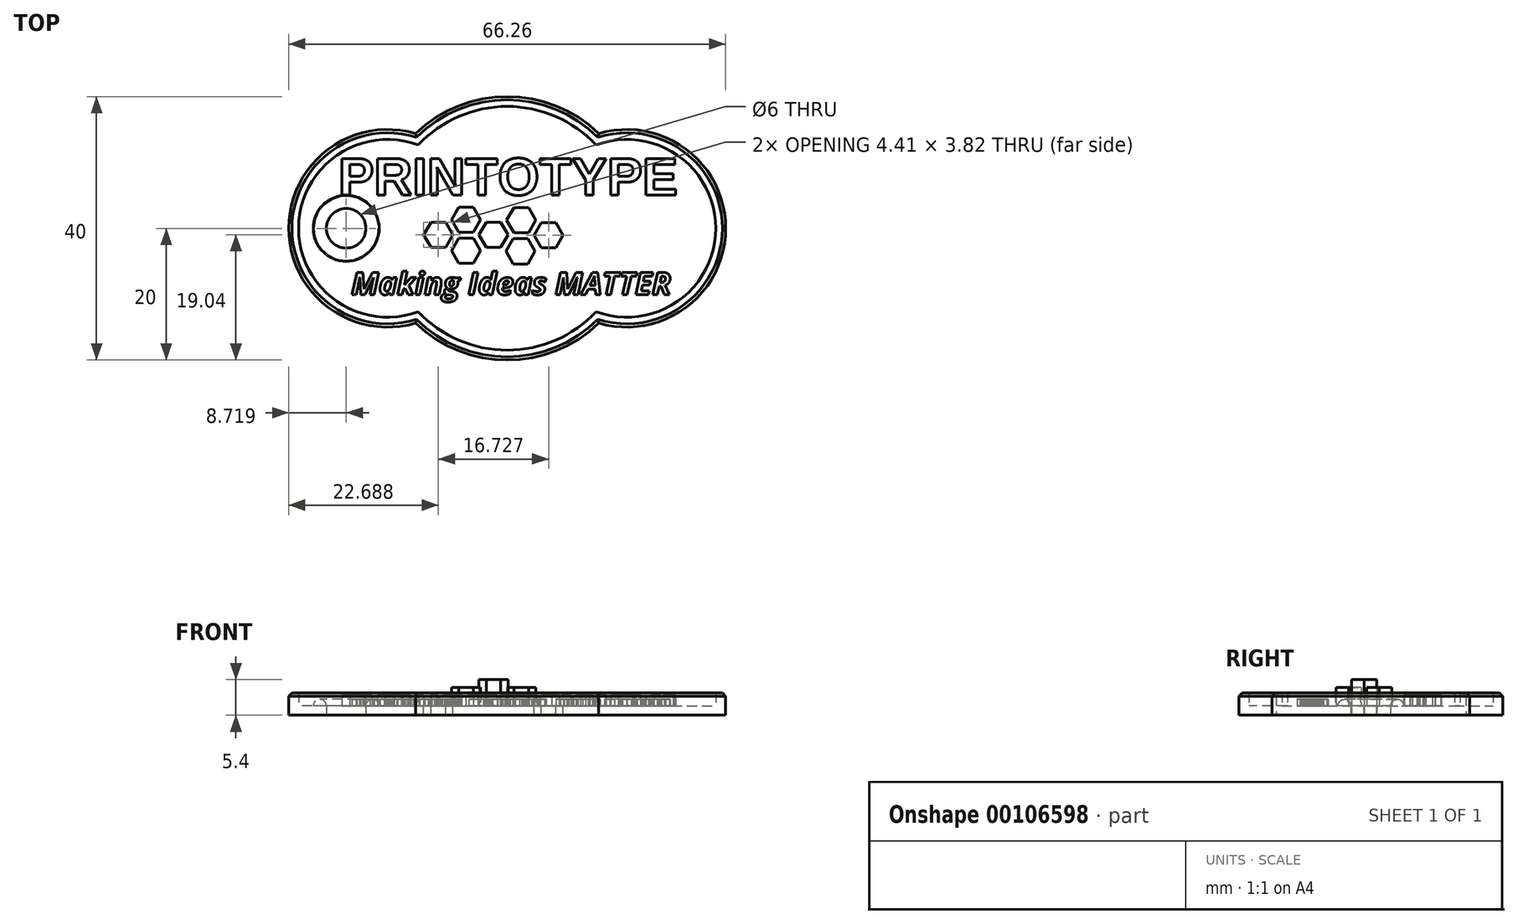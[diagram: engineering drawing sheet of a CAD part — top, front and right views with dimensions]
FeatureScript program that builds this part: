
annotation { "Feature Type Name" : "Feature", "Feature Type Description" : "" }
export const myFeature = defineFeature(function(context is Context, id is Id, definition is map)
    precondition{}
    {
        {
            var Q0;
            Q0=qCreatedBy(makeId("Top.planeOp"),FACE);
            var sketch = newSketch(context, id + "F0", { "sketchPlane" : qUnion([Q0])});
            skArc(sketch, "E0", {"start": v(-13.9, 14.39) * mm, "mid": v(-33.13, 0) * mm, "end": v(-13.9, -14.39) * mm});
            skLineSegment(sketch, "E1", {"start": v(0, 0) * mm, "end": v(0, 52.6) * mm});
            skArc(sketch, "E2.MirrorC", {"start": v(13.9, 14.39) * mm, "mid": v(33.13, 0) * mm, "end": v(13.9, -14.39) * mm});
            skCircle(sketch, "E3", {"center": v(-24.41, 0) * mm, "radius": 3 * mm});
            skCircle(sketch, "E4", {"center": v(-24.41, 0) * mm, "radius": 5 * mm});
            skArc(sketch, "E5", {"start": v(-13.48, 12.67) * mm, "mid": v(-31.63, 0) * mm, "end": v(-13.48, -12.67) * mm});
            skArc(sketch, "E6", {"start": v(13.48, -12.67) * mm, "mid": v(31.63, 0) * mm, "end": v(13.48, 12.67) * mm});
            skArc(sketch, "E7", {"start": v(-13.48, -12.67) * mm, "mid": v(0, -18.5) * mm, "end": v(13.48, -12.67) * mm});
            skArc(sketch, "E8.trimOffspring", {"start": v(-13.9, -14.39) * mm, "mid": v(0, -20) * mm, "end": v(13.9, -14.39) * mm});
            skArc(sketch, "E9.trimOffspring", {"start": v(13.48, 12.67) * mm, "mid": v(0, 18.5) * mm, "end": v(-13.48, 12.67) * mm});
            skArc(sketch, "E10.trimOffspring", {"start": v(13.9, 14.39) * mm, "mid": v(0, 20) * mm, "end": v(-13.9, 14.39) * mm});
            skSolve(sketch);
        }
        {
            var Q0;
            Q0=qCreatedBy(makeId("Top.planeOp"),FACE);
            var sketch = newSketch(context, id + "F1", { "sketchPlane" : qUnion([Q0])});
            skText(sketch, "E11", { "text": "PRINTOTYPE", "fontName": "Arimo-Bold.ttf"});
            const initialGuessF1  = {"E11": [-0.02558, 0.00505, 1, 0, 0.0058]};
            skSetInitialGuess(sketch, initialGuessF1);
            skSolve(sketch);
        }
        {
            var Q0;
            Q0=qCreatedBy(makeId("Top.planeOp"),FACE);
            var sketch = newSketch(context, id + "F2", { "sketchPlane" : qUnion([Q0])});
            skText(sketch, "E12", { "text": "Making Ideas MATTER", "fontName": "OpenSans-BoldItalic.ttf"});
            const initialGuessF2  = {"E12": [-0.02364, -0.01007, 1, 0, 0.0034]};
            skSetInitialGuess(sketch, initialGuessF2);
            skSolve(sketch);
        }
        {
            var Q0;
            Q0=makeQuery(id+"F0.imprint","IMPRINT",FACE,{"disambiguationData":[TD([[makeQuery(id+"F0.imprint","IMPRINT",EDGE,{"derivedFrom":sQuery(id+"F0.wireOp",EDGE,"E4")}),-1.0]])]});
            var Q1;
            {var subQ5=sQuery(id+"F0.wireOp",EDGE,"E0");Q1=makeQuery(id+"F0.imprint","IMPRINT",FACE,{"disambiguationData":[TD([[makeQuery(id+"F0.imprint","IMPRINT",EDGE,{"derivedFrom":subQ5}),1.0]])]});}
            var Q2;
            Q2=makeQuery(id+"F0.imprint","IMPRINT",FACE,{"disambiguationData":[TD([[makeQuery(id+"F0.imprint","IMPRINT",EDGE,{"derivedFrom":sQuery(id+"F0.wireOp",EDGE,"E3")}),-1.0]])]});
            extrude(context, id + "F3", {"entities" : qUnion([Q0, Q1, Q2]), "depth" : 1.4 * mm});
        }
        {
            var Q0;
            Q0=makeQuery(id+"F0.imprint","IMPRINT",FACE,{"disambiguationData":[TD([[makeQuery(id+"F0.imprint","IMPRINT",EDGE,{"derivedFrom":sQuery(id+"F0.wireOp",EDGE,"E3")}),-1.0]])]});
            var Q1;
            {var subQ5=sQuery(id+"F0.wireOp",EDGE,"E0");Q1=makeQuery(id+"F0.imprint","IMPRINT",FACE,{"disambiguationData":[TD([[makeQuery(id+"F0.imprint","IMPRINT",EDGE,{"derivedFrom":subQ5}),1.0]])]});}
            extrude(context, id + "F4", {"entities" : qUnion([Q0, Q1]), "operationType" : NewBodyOperationType.ADD, "depth" : 3.4 * mm});
        }
        {
            var Q0;
            Q0=makeQuery(id+"F4.opExtrude","CAP_EDGE",EDGE,{"disambiguationData":[OSD([sQuery(id+"F0.wireOp",EDGE,"E4")])],"isStart":false});
            fillet(context, id + "F5", {"entities" : qUnion([Q0]), "radius" : 2 * mm, "tangentPropagation" : true, "allowEdgeOverflow" : false});
        }
        {
            var Q0;
            {var subQ0=sQuery(id+"F0.wireOp",EDGE,"E3");Q0=makeQuery(id+"F5.opFillet","BLEND_EDGE",EDGE,{"blendedFrom":[makeQuery(id+"F4.opExtrude","CAP_EDGE",EDGE,{"disambiguationData":[OSD([sQuery(id+"F0.wireOp",EDGE,"E4")])],"isStart":false}),makeQuery(id+"F4.boolean.opBoolean","MERGE",FACE,{"derivedFrom":[makeQuery(id+"F3.opExtrude","SWEPT_FACE",FACE,{"disambiguationData":[OSD([subQ0])]}),makeQuery(id+"F4.opExtrude","SWEPT_FACE",FACE,{"disambiguationData":[OSD([subQ0])]})]})],"blendedInto":[makeQuery(id+"F4.boolean.opBoolean","MERGE",FACE,{"derivedFrom":[makeQuery(id+"F3.opExtrude","SWEPT_FACE",FACE,{"disambiguationData":[OSD([subQ0])]}),makeQuery(id+"F4.opExtrude","SWEPT_FACE",FACE,{"disambiguationData":[OSD([subQ0])]})]})]});}
            fillet(context, id + "F6", {"entities" : qUnion([Q0]), "radius" : 1 * mm, "tangentPropagation" : true, "allowEdgeOverflow" : false});
        }
        {
            var Q0;
            Q0 = qSketchRegion(id + "F1", true);
            extrude(context, id + "F7", {"entities" : qUnion([Q0]), "operationType" : NewBodyOperationType.ADD, "depth" : 3 * mm});
        }
        {
            var Q0;
            Q0 = qSketchRegion(id + "F2", true);
            extrude(context, id + "F8", {"entities" : qUnion([Q0]), "operationType" : NewBodyOperationType.ADD, "depth" : 2.4 * mm});
        }
        {
            var Q0;
            {var subQ36=makeQuery(id+"F4.opExtrude","SWEPT_FACE",FACE,{"disambiguationData":[OSD([sQuery(id+"F0.wireOp",EDGE,"E5")])]});var subQ58=sQuery(id+"F0.wireOp",EDGE,"E3");Q0=makeQuery(id+"F8.boolean.opBoolean","SPLIT",FACE,{"disambiguationData":[TD([subQ36])],"derivedFrom":makeQuery(id+"F7.boolean.opBoolean","SPLIT",FACE,{"disambiguationData":[TD([subQ36])],"derivedFrom":makeQuery(id+"F3.opExtrude","CAP_FACE",FACE,{"disambiguationData":[OSD([sQuery(id+"F0.wireOp",EDGE,"E0"),sQuery(id+"F0.wireOp",EDGE,"E2.MirrorC"),subQ58,sQuery(id+"F0.wireOp",EDGE,"E8.trimOffspring"),sQuery(id+"F0.wireOp",EDGE,"E10.trimOffspring")])],"isStart":false})})});}
            var sketch = newSketch(context, id + "F9", { "sketchPlane" : qUnion([Q0])});
            skCircle(sketch, "E13.cCircle", {"center": v(-10.44, -0.96) * mm, "radius": 1.91 * mm, "construction": true});
            skLineSegment(sketch, "E13.0", {"start": v(-11.55, 0.95) * mm, "end": v(-9.34, 0.95) * mm});
            skLineSegment(sketch, "E13.1", {"start": v(-9.34, 0.95) * mm, "end": v(-8.24, -0.96) * mm});
            skLineSegment(sketch, "E13.2", {"start": v(-8.24, -0.96) * mm, "end": v(-9.34, -2.87) * mm});
            skLineSegment(sketch, "E13.3", {"start": v(-9.34, -2.87) * mm, "end": v(-11.55, -2.87) * mm});
            skLineSegment(sketch, "E13.4", {"start": v(-11.55, -2.87) * mm, "end": v(-12.65, -0.96) * mm});
            skLineSegment(sketch, "E13.5", {"start": v(-12.65, -0.96) * mm, "end": v(-11.55, 0.95) * mm});
            skPoint(sketch, "E13.0.midPoint", {"position": v(-10.44, 0.95) * mm});
            skCircle(sketch, "E14.cCircle", {"center": v(-6.24, 1.29) * mm, "radius": 1.91 * mm, "construction": true});
            skLineSegment(sketch, "E14.0", {"start": v(-7.34, 3.2) * mm, "end": v(-5.13, 3.2) * mm});
            skLineSegment(sketch, "E14.1", {"start": v(-5.13, 3.2) * mm, "end": v(-4.03, 1.29) * mm});
            skLineSegment(sketch, "E14.2", {"start": v(-4.03, 1.29) * mm, "end": v(-5.13, -0.63) * mm});
            skLineSegment(sketch, "E14.3", {"start": v(-5.13, -0.63) * mm, "end": v(-7.34, -0.63) * mm});
            skLineSegment(sketch, "E14.4", {"start": v(-7.34, -0.63) * mm, "end": v(-8.44, 1.29) * mm});
            skLineSegment(sketch, "E14.5", {"start": v(-8.44, 1.29) * mm, "end": v(-7.34, 3.2) * mm});
            skPoint(sketch, "E14.0.midPoint", {"position": v(-6.24, 3.2) * mm});
            skCircle(sketch, "E15.cCircle", {"center": v(-6.24, -3.4) * mm, "radius": 1.91 * mm, "construction": true});
            skLineSegment(sketch, "E15.0", {"start": v(-7.34, -1.49) * mm, "end": v(-5.13, -1.49) * mm});
            skLineSegment(sketch, "E15.1", {"start": v(-5.13, -1.49) * mm, "end": v(-4.03, -3.4) * mm});
            skLineSegment(sketch, "E15.2", {"start": v(-4.03, -3.4) * mm, "end": v(-5.13, -5.3) * mm});
            skLineSegment(sketch, "E15.3", {"start": v(-5.13, -5.3) * mm, "end": v(-7.34, -5.3) * mm});
            skLineSegment(sketch, "E15.4", {"start": v(-7.34, -5.3) * mm, "end": v(-8.44, -3.4) * mm});
            skLineSegment(sketch, "E15.5", {"start": v(-8.44, -3.4) * mm, "end": v(-7.34, -1.49) * mm});
            skPoint(sketch, "E15.0.midPoint", {"position": v(-6.24, -1.49) * mm});
            skCircle(sketch, "E16.cCircle", {"center": v(-2.08, -1) * mm, "radius": 1.91 * mm, "construction": true});
            skLineSegment(sketch, "E16.0", {"start": v(-3.18, 0.9) * mm, "end": v(-0.98, 0.9) * mm});
            skLineSegment(sketch, "E16.1", {"start": v(-0.98, 0.9) * mm, "end": v(0.13, -1) * mm});
            skLineSegment(sketch, "E16.2", {"start": v(0.13, -1) * mm, "end": v(-0.98, -2.92) * mm});
            skLineSegment(sketch, "E16.3", {"start": v(-0.98, -2.92) * mm, "end": v(-3.18, -2.92) * mm});
            skLineSegment(sketch, "E16.4", {"start": v(-3.18, -2.92) * mm, "end": v(-4.29, -1) * mm});
            skLineSegment(sketch, "E16.5", {"start": v(-4.29, -1) * mm, "end": v(-3.18, 0.9) * mm});
            skPoint(sketch, "E16.0.midPoint", {"position": v(-2.08, 0.9) * mm});
            skCircle(sketch, "E17.cCircle", {"center": v(2.03, -3.5) * mm, "radius": 1.91 * mm, "construction": true});
            skLineSegment(sketch, "E17.0", {"start": v(0.93, -1.58) * mm, "end": v(3.14, -1.58) * mm});
            skLineSegment(sketch, "E17.1", {"start": v(3.14, -1.58) * mm, "end": v(4.24, -3.5) * mm});
            skLineSegment(sketch, "E17.2", {"start": v(4.24, -3.5) * mm, "end": v(3.14, -5.4) * mm});
            skLineSegment(sketch, "E17.3", {"start": v(3.14, -5.4) * mm, "end": v(0.93, -5.4) * mm});
            skLineSegment(sketch, "E17.4", {"start": v(0.93, -5.4) * mm, "end": v(-0.18, -3.5) * mm});
            skLineSegment(sketch, "E17.5", {"start": v(-0.18, -3.5) * mm, "end": v(0.93, -1.58) * mm});
            skPoint(sketch, "E17.0.midPoint", {"position": v(2.03, -1.58) * mm});
            skCircle(sketch, "E18.cCircle", {"center": v(2.13, 1.24) * mm, "radius": 1.91 * mm, "construction": true});
            skLineSegment(sketch, "E18.0", {"start": v(1.02, 3.15) * mm, "end": v(3.23, 3.15) * mm});
            skLineSegment(sketch, "E18.1", {"start": v(3.23, 3.15) * mm, "end": v(4.33, 1.24) * mm});
            skLineSegment(sketch, "E18.2", {"start": v(4.33, 1.24) * mm, "end": v(3.23, -0.67) * mm});
            skLineSegment(sketch, "E18.3", {"start": v(3.23, -0.67) * mm, "end": v(1.02, -0.67) * mm});
            skLineSegment(sketch, "E18.4", {"start": v(1.02, -0.67) * mm, "end": v(-0.08, 1.24) * mm});
            skLineSegment(sketch, "E18.5", {"start": v(-0.08, 1.24) * mm, "end": v(1.02, 3.15) * mm});
            skPoint(sketch, "E18.0.midPoint", {"position": v(2.13, 3.15) * mm});
            skCircle(sketch, "E19.cCircle", {"center": v(6.29, -1.05) * mm, "radius": 1.91 * mm, "construction": true});
            skLineSegment(sketch, "E19.0", {"start": v(5.18, 0.86) * mm, "end": v(7.39, 0.86) * mm});
            skLineSegment(sketch, "E19.1", {"start": v(7.39, 0.86) * mm, "end": v(8.5, -1.05) * mm});
            skLineSegment(sketch, "E19.2", {"start": v(8.5, -1.05) * mm, "end": v(7.39, -2.96) * mm});
            skLineSegment(sketch, "E19.3", {"start": v(7.39, -2.96) * mm, "end": v(5.18, -2.96) * mm});
            skLineSegment(sketch, "E19.4", {"start": v(5.18, -2.96) * mm, "end": v(4.08, -1.05) * mm});
            skLineSegment(sketch, "E19.5", {"start": v(4.08, -1.05) * mm, "end": v(5.18, 0.86) * mm});
            skPoint(sketch, "E19.0.midPoint", {"position": v(6.29, 0.86) * mm});
            skSolve(sketch);
        }
        {
            var Q0;
            Q0=makeQuery(id+"F9.imprint","IMPRINT",FACE,{"disambiguationData":[TD([[makeQuery(id+"F9.imprint","IMPRINT",EDGE,{"derivedFrom":sQuery(id+"F9.wireOp",EDGE,"E13.0")}),-1.0]])]});
            var Q1;
            Q1=makeQuery(id+"F9.imprint","IMPRINT",FACE,{"disambiguationData":[TD([[makeQuery(id+"F9.imprint","IMPRINT",EDGE,{"derivedFrom":sQuery(id+"F9.wireOp",EDGE,"E19.0")}),-1.0]])]});
            extrude(context, id + "F10", {"entities" : qUnion([Q0, Q1]), "operationType" : NewBodyOperationType.REMOVE, "oppositeDirection" : true, "depth" : 25 * mm});
        }
        {
            var Q0;
            Q0=makeQuery(id+"F9.imprint","IMPRINT",FACE,{"disambiguationData":[TD([[makeQuery(id+"F9.imprint","IMPRINT",EDGE,{"derivedFrom":sQuery(id+"F9.wireOp",EDGE,"E14.0")}),-1.0]])]});
            var Q1;
            Q1=makeQuery(id+"F9.imprint","IMPRINT",FACE,{"disambiguationData":[TD([[makeQuery(id+"F9.imprint","IMPRINT",EDGE,{"derivedFrom":sQuery(id+"F9.wireOp",EDGE,"E17.0")}),-1.0]])]});
            extrude(context, id + "F11", {"entities" : qUnion([Q0, Q1]), "operationType" : NewBodyOperationType.ADD, "depth" : 2 * mm});
        }
        {
            var Q0;
            Q0=makeQuery(id+"F9.imprint","IMPRINT",FACE,{"disambiguationData":[TD([[makeQuery(id+"F9.imprint","IMPRINT",EDGE,{"derivedFrom":sQuery(id+"F9.wireOp",EDGE,"E16.0")}),-1.0]])]});
            extrude(context, id + "F12", {"entities" : qUnion([Q0]), "operationType" : NewBodyOperationType.ADD, "depth" : 4 * mm});
        }
        {
            var Q0;
            Q0=makeQuery(id+"F9.imprint","IMPRINT",FACE,{"disambiguationData":[TD([[makeQuery(id+"F9.imprint","IMPRINT",EDGE,{"derivedFrom":sQuery(id+"F9.wireOp",EDGE,"E15.0")}),-1.0]])]});
            var Q1;
            Q1=makeQuery(id+"F9.imprint","IMPRINT",FACE,{"disambiguationData":[TD([[makeQuery(id+"F9.imprint","IMPRINT",EDGE,{"derivedFrom":sQuery(id+"F9.wireOp",EDGE,"E18.0")}),-1.0]])]});
            extrude(context, id + "F13", {"entities" : qUnion([Q0, Q1]), "operationType" : NewBodyOperationType.ADD, "depth" : 2.8 * mm});
        }
        {
            var Q0;
            Q0=makeQuery(id+"F4.opExtrude","CAP_EDGE",EDGE,{"disambiguationData":[OSD([sQuery(id+"F0.wireOp",EDGE,"E0")])],"isStart":false});
            var Q1;
            Q1=makeQuery(id+"F4.opExtrude","CAP_EDGE",EDGE,{"disambiguationData":[OSD([sQuery(id+"F0.wireOp",EDGE,"E2.MirrorC")])],"isStart":false});
            var Q2;
            Q2=makeQuery(id+"F4.opExtrude","CAP_EDGE",EDGE,{"disambiguationData":[OSD([sQuery(id+"F0.wireOp",EDGE,"E8.trimOffspring")])],"isStart":false});
            var Q3;
            Q3=makeQuery(id+"F4.opExtrude","CAP_EDGE",EDGE,{"disambiguationData":[OSD([sQuery(id+"F0.wireOp",EDGE,"E10.trimOffspring")])],"isStart":false});
            chamfer(context, id + "F14", {"entities" : qUnion([Q0, Q1, Q2, Q3]), "width" : .5 * mm, "tangentPropagation" : true});
        }
    });
